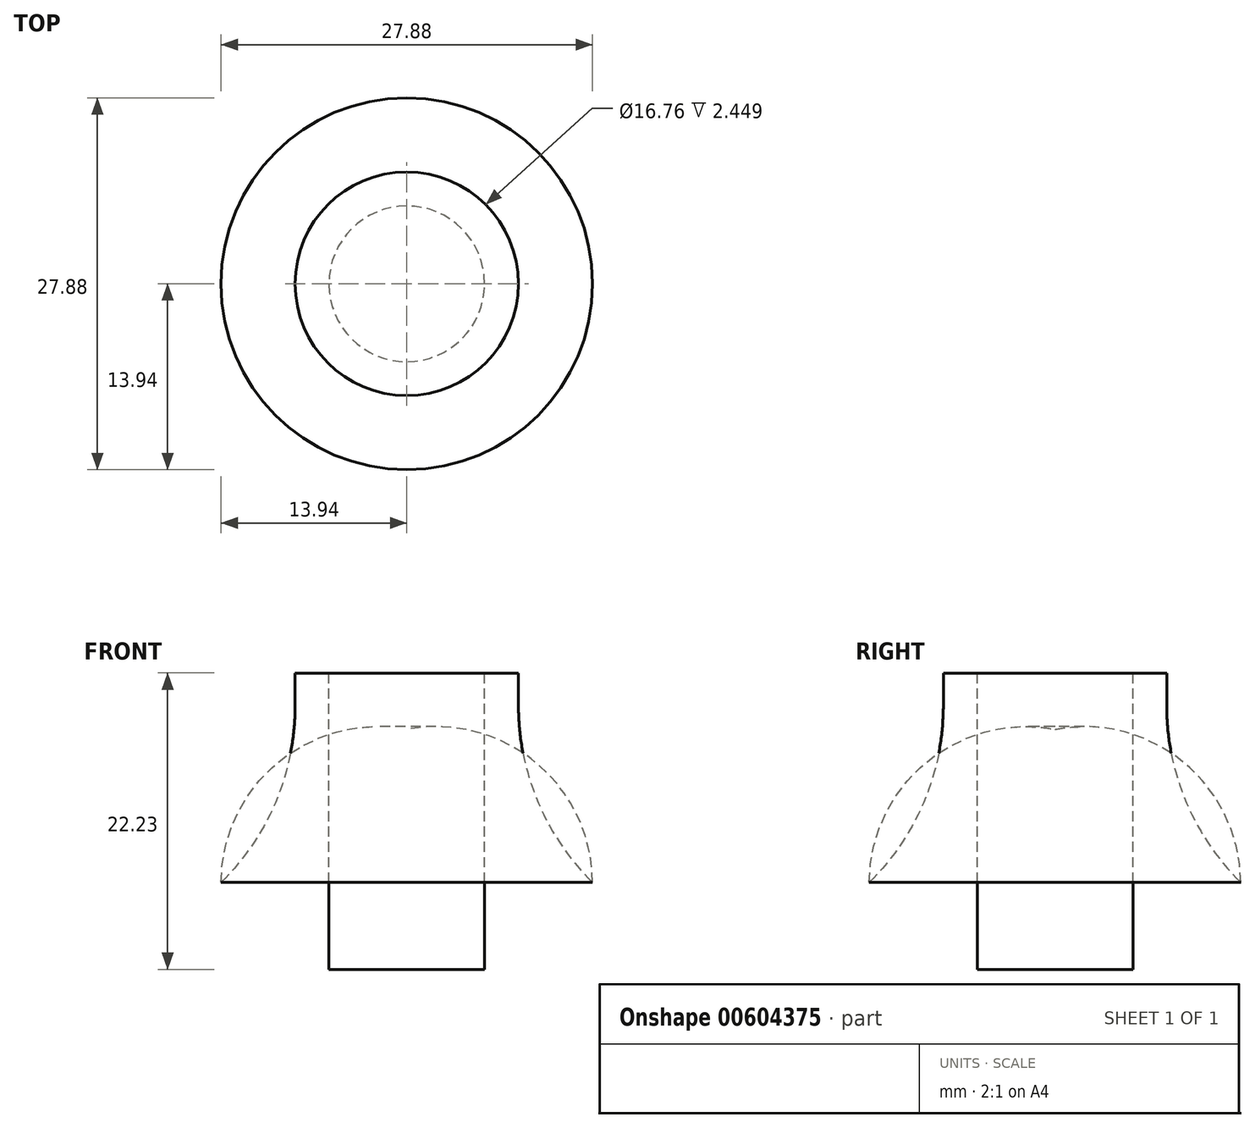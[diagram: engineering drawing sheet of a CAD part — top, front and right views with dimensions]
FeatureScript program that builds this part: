
annotation { "Feature Type Name" : "Feature", "Feature Type Description" : "" }
export const myFeature = defineFeature(function(context is Context, id is Id, definition is map)
    precondition{}
    {
        {
            var Q0;
            Q0=qCreatedBy(makeId("Right.planeOp"),FACE);
            var sketch = newSketch(context, id + "F0", { "sketchPlane" : qUnion([Q0])});
            skLineSegment(sketch, "E0", {"start": v(-5.84, 27.3) * mm, "end": v(-5.84, 5.08) * mm});
            skLineSegment(sketch, "E1", {"start": v(-5.84, 5.08) * mm, "end": v(0, 5.08) * mm});
            skLineSegment(sketch, "E2", {"start": v(0, 5.08) * mm, "end": v(0, 0) * mm});
            skLineSegment(sketch, "E3", {"start": v(-8.38, 27.3) * mm, "end": v(-5.84, 27.3) * mm});
            skLineSegment(sketch, "E4", {"start": v(-8.38, 27.3) * mm, "end": v(-8.38, 24.86) * mm});
            skArc(sketch, "E5", {"start": v(-13.94, 11.6) * mm, "mid": v(-9.83, 17.66) * mm, "end": v(-8.38, 24.86) * mm});
            skArc(sketch, "E6", {"start": v(-13.94, 11.6) * mm, "mid": v(-9.7, 2.5) * mm, "end": v(0, 0) * mm});
            skSolve(sketch);
        }
        {
            var Q0;
            Q0=makeQuery(id+"F0.imprint","IMPRINT",FACE,{"disambiguationData":[TD([[makeQuery(id+"F0.imprint","IMPRINT",EDGE,{"derivedFrom":sQuery(id+"F0.wireOp",EDGE,"E0")}),-1.0]])]});
            var Q1;
            Q1=sQuery(id+"F0.wireOp",EDGE,"E2");
            revolve(context, id + "F1", {"entities" : qUnion([Q0]), "axis" : qUnion([Q1]), "revolveType" : RevolveType.FULL});
        }
    });
